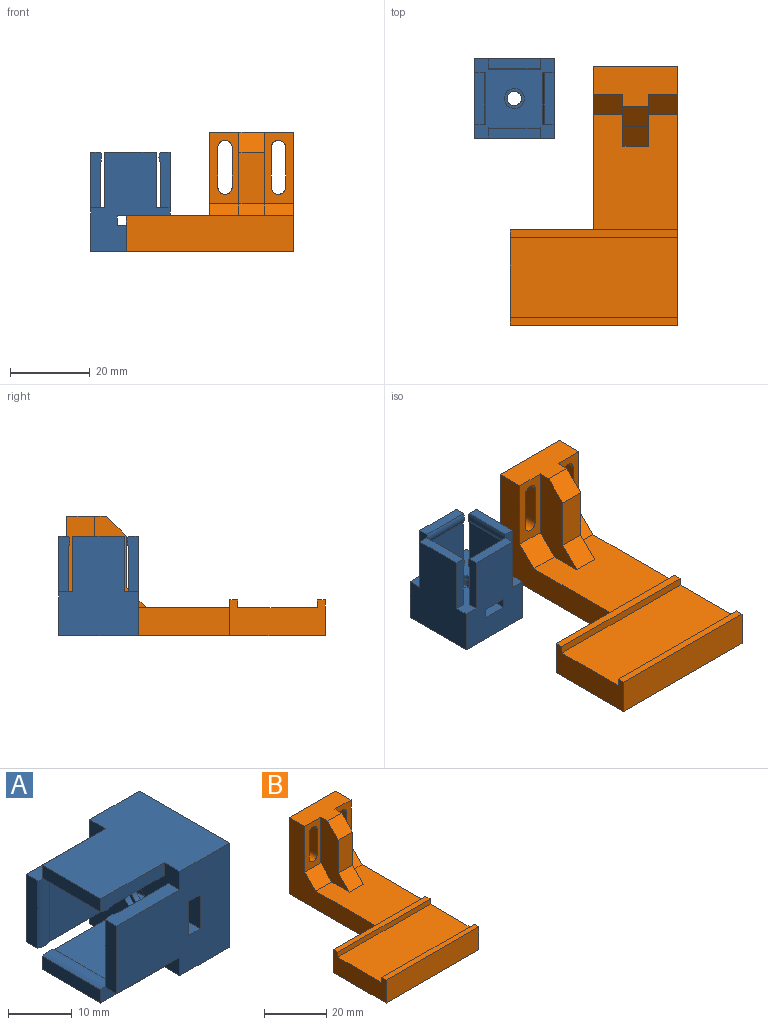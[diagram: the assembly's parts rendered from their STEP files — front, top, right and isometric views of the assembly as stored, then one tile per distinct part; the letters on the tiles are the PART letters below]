
ASSEMBLY  parts=2 mates=1
PART A: 34 faces, bbox 25x20x20 mm
  f0: cylinder r=1.8mm len=3.6mm, axis (1,0,0), area 11.3mm2, adj f13,f17
  f1: plane 25x20mm, normal (0,1,0), area 385.8mm2, adj f4,f5,f6,f7,f14,f15,f16,f17
  f2: plane 25x20mm, normal (0,-1,0), area 385.8mm2, adj f4,f5,f6,f7,f14,f15,f16,f17
  f3: cylinder r=1.8mm len=6.5mm, axis (1,0,0), area 73.5mm2, adj f7,f15
  f4: plane 25x20mm, normal (0,0,1), area 402mm2, adj f1,f2,f6,f7,f24,f26,f27
  f5: plane 25x20mm, normal (0,0,-1), area 402mm2, adj f1,f2,f6,f7,f8,f10,f11
  f6: plane 20x20mm, normal (-1,0,0), area 250.4mm2, adj f1,f2,f4,f5,f8,f9,f10,f12
  f7: plane 20x20mm, normal (1,0,0), area 389.8mm2, adj f1,f2,f3,f4,f5
  f8: plane 14x2.8mm, normal (0,-1,0), area 35.5mm2, adj f5,f6,f9,f11,f18
  f9: plane 13x11.38mm, normal (0,0,1), area 148mm2, adj f6,f8,f10,f18
  f10: plane 14x2.8mm, normal (0,1,0), area 35.5mm2, adj f5,f6,f9,f11,f18
  f11: plane 13x2.5mm, normal (-1,0,0), area 32.5mm2, adj f5,f8,f10,f18
  f12: cylinder r=2.5mm len=5mm, axis (-1,0,0), area 15.7mm2, adj f6,f13
  f13: plane 5x5mm, normal (-1,0,0), area 9.5mm2, adj f0,f12
  f14: plane 20x2.5mm, normal (0,0,1), area 50mm2, adj f1,f2,f15,f17
  f15: plane 20x6.5mm, normal (-1,0,0), area 119.8mm2, adj f1,f2,f3,f14,f16
  f16: plane 20x2.5mm, normal (0,0,-1), area 50mm2, adj f1,f2,f15,f17
  f17: plane 20x6.5mm, normal (1,0,0), area 119.8mm2, adj f0,f1,f2,f14,f16
  f18: cylinder r=3mm len=13mm, axis (0,-1,0), area 35.2mm2, adj f8,f9,f10,f11
  f19: plane 14x2.8mm, normal (0,0,1), area 35.5mm2, adj f2,f6,f20,f22,f23
  f20: plane 13x11.38mm, normal (0,1,0), area 148mm2, adj f6,f19,f21,f23
  f21: plane 14x2.8mm, normal (0,0,-1), area 35.5mm2, adj f2,f6,f20,f22,f23
  f22: plane 13x2.5mm, normal (-1,0,0), area 32.5mm2, adj f2,f19,f21,f23
  f23: cylinder r=3mm len=13mm, axis (0,0,1), area 35.2mm2, adj f19,f20,f21,f22
  f24: plane 14x2.8mm, normal (0,1,0), area 35.5mm2, adj f4,f6,f25,f27,f28
  f25: plane 13x11.38mm, normal (0,0,-1), area 148mm2, adj f6,f24,f26,f28
  f26: plane 14x2.8mm, normal (0,-1,0), area 35.5mm2, adj f4,f6,f25,f27,f28
  f27: plane 13x2.5mm, normal (-1,0,0), area 32.5mm2, adj f4,f24,f26,f28
  f28: cylinder r=3mm len=13mm, axis (0,1,0), area 35.2mm2, adj f24,f25,f26,f27
  f29: plane 14x2.8mm, normal (0,0,-1), area 35.5mm2, adj f1,f6,f30,f32,f33
  f30: plane 13x11.38mm, normal (0,-1,0), area 148mm2, adj f6,f29,f31,f33
  f31: plane 14x2.8mm, normal (0,0,1), area 35.5mm2, adj f1,f6,f30,f32,f33
  f32: plane 13x2.5mm, normal (-1,0,0), area 32.5mm2, adj f1,f29,f31,f33
  f33: cylinder r=3mm len=13mm, axis (0,0,-1), area 35.2mm2, adj f29,f30,f31,f32
PART B: 31 faces, bbox 42x65x30 mm
  f0: plane 42x20mm, normal (0,0,1), area 840mm2, adj f7,f26,f27,f30
  f1: plane 29x21mm, normal (0,0,1), area 557.8mm2, adj f7,f12,f15,f16,f18,f23,f24,f25
  f2: plane 30x21mm, normal (0,1,0), area 537.6mm2, adj f3,f6,f7,f8,f9,f10,f11,f18
  f3: plane 21x10mm, normal (0,0,1), area 166.2mm2, adj f2,f4,f7,f12,f14,f17,f18,f23
  f4: plane 18x7.3mm, normal (0,-1,0), area 85.2mm2, adj f3,f7,f8,f9,f10,f11,f12,f16
  f5: plane 42x9mm, normal (0,-1,0), area 378mm2, adj f6,f7,f29,f30
  f6: plane 65x42mm, normal (0,0,-1), area 1869mm2, adj f2,f5,f7,f18,f25,f30
  f7: plane 65x30mm, normal (1,0,0), area 636.5mm2, adj f0,f1,f2,f3,f4,f5,f6,f16
  f8: plane 10x7mm, normal (-1,0,0), area 70mm2, adj f2,f4,f9,f11
  f9: cylinder r=1.8mm len=7mm, axis (0,1,0), area 39.6mm2, adj f2,f4,f8,f10
  f10: plane 10x7mm, normal (1,0,0), area 70mm2, adj f2,f4,f9,f11
  f11: cylinder r=1.8mm len=7mm, axis (0,1,0), area 39.6mm2, adj f2,f4,f8,f10
  f12: plane 23x13mm, normal (1,0,0), area 171.5mm2, adj f1,f3,f4,f13,f14,f15,f16
  f13: plane 13x6.4mm, normal (0,-1,0), area 83.2mm2, adj f12,f14,f15,f23
  f14: plane 6.4x5mm, normal (0,-0.71,0.71), area 45.3mm2, adj f3,f12,f13,f23
  f15: plane 6.4x5mm, normal (0,-0.71,0.71), area 45.3mm2, adj f1,f12,f13,f23
  f16: plane 7.3x5mm, normal (0,-0.71,0.71), area 51.6mm2, adj f1,f4,f7,f12
  f17: plane 18x7.3mm, normal (0,-1,0), area 85.2mm2, adj f3,f18,f19,f20,f21,f22,f23,f24
  f18: plane 41x30mm, normal (-1,0,0), area 460.5mm2, adj f1,f2,f3,f6,f17,f24,f25
  f19: plane 10x7mm, normal (1,0,0), area 70mm2, adj f2,f17,f20,f22
  f20: cylinder r=1.8mm len=7mm, axis (0,1,0), area 39.6mm2, adj f2,f17,f19,f21
  f21: plane 10x7mm, normal (-1,0,0), area 70mm2, adj f2,f17,f20,f22
  f22: cylinder r=1.8mm len=7mm, axis (0,1,0), area 39.6mm2, adj f2,f17,f19,f21
  f23: plane 23x13mm, normal (-1,0,0), area 171.5mm2, adj f1,f3,f13,f14,f15,f17,f24
  f24: plane 7.3x5mm, normal (0,-0.71,0.71), area 51.6mm2, adj f1,f17,f18,f23
  f25: plane 42x9mm, normal (0,1,0), area 231mm2, adj f1,f6,f7,f18,f28,f30
  f26: plane 42x2mm, normal (0,1,0), area 84mm2, adj f0,f7,f29,f30
  f27: plane 42x2mm, normal (0,-1,0), area 84mm2, adj f0,f7,f28,f30
  f28: plane 42x2mm, normal (0,0,1), area 84mm2, adj f7,f25,f27,f30
  f29: plane 42x2mm, normal (0,0,1), area 84mm2, adj f5,f7,f26,f30
  f30: plane 24x9mm, normal (-1,0,0), area 176mm2, adj f0,f5,f6,f25,f26,f27,f28,f29
PLACE A rot(axis=(-0.71,0,0.71),180deg) t=(-50.5,1.19,-18.89)mm
PLACE B t=(-20,2.19,11.11)mm fixed
MATE planar A.f0 <-> B.f6  axis (0,0,-1) through (-50.5,1.19,-18.89)mm
